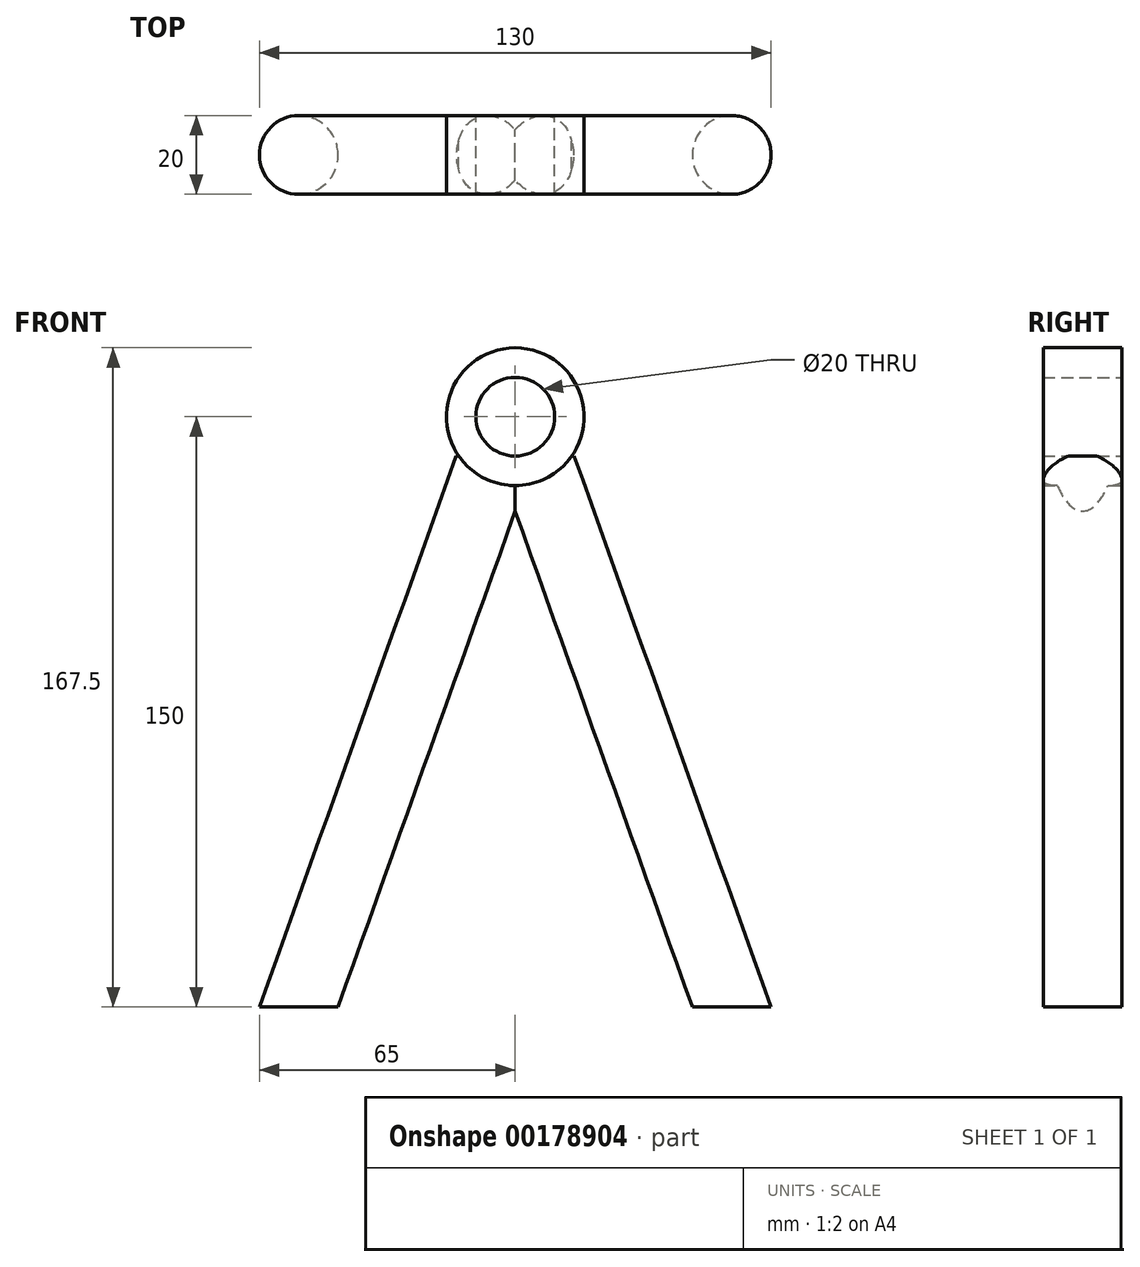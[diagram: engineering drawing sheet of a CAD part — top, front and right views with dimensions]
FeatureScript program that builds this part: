
annotation { "Feature Type Name" : "Feature", "Feature Type Description" : "" }
export const myFeature = defineFeature(function(context is Context, id is Id, definition is map)
    precondition{}
    {
        {
            var Q0;
            Q0=qCreatedBy(makeId("Top.planeOp"),FACE);
            var sketch = newSketch(context, id + "F0", { "sketchPlane" : qUnion([Q0])});
            skCircle(sketch, "E0", {"center": v(-55, 0) * mm, "radius": 10 * mm});
            skCircle(sketch, "E1", {"center": v(55, 0) * mm, "radius": 10 * mm});
            skSolve(sketch);
        }
        {
            var Q0;
            Q0=qCreatedBy(makeId("Front.planeOp"),FACE);
            var sketch = newSketch(context, id + "F1", { "sketchPlane" : qUnion([Q0])});
            skLineSegment(sketch, "E2", {"start": v(-55, 0) * mm, "end": v(-5, 140) * mm});
            skLineSegment(sketch, "E3", {"start": v(55, 0) * mm, "end": v(5, 140) * mm});
            skSolve(sketch);
        }
        {
            var Q0;
            Q0=makeQuery(id+"F0.imprint","IMPRINT",FACE,{"disambiguationData":[TD([[makeQuery(id+"F0.imprint","IMPRINT",EDGE,{"derivedFrom":sQuery(id+"F0.wireOp",EDGE,"E0")}),1.0]])]});
            var Q1;
            Q1=sQuery(id+"F1.wireOp",EDGE,"E2");
            sweep(context, id + "F2", {"profiles" : qUnion([Q0]), "path" : qUnion([Q1])});
        }
        {
            var Q0;
            Q0=makeQuery(id+"F0.imprint","IMPRINT",FACE,{"disambiguationData":[TD([[makeQuery(id+"F0.imprint","IMPRINT",EDGE,{"derivedFrom":sQuery(id+"F0.wireOp",EDGE,"E1")}),1.0]])]});
            var Q1;
            Q1=sQuery(id+"F1.wireOp",EDGE,"E3");
            sweep(context, id + "F3", {"operationType" : NewBodyOperationType.ADD, "profiles" : qUnion([Q0]), "path" : qUnion([Q1])});
        }
        {
            var Q0;
            Q0=qCreatedBy(makeId("Front.planeOp"),FACE);
            var sketch = newSketch(context, id + "F4", { "sketchPlane" : qUnion([Q0])});
            skCircle(sketch, "E4", {"center": v(0, 150) * mm, "radius": 17.5 * mm});
            skCircle(sketch, "E5", {"center": v(0, 150) * mm, "radius": 10 * mm});
            skSolve(sketch);
        }
        {
            var Q0;
            Q0=makeQuery(id+"F4.imprint","IMPRINT",FACE,{"disambiguationData":[TD([[makeQuery(id+"F4.imprint","IMPRINT",EDGE,{"derivedFrom":sQuery(id+"F4.wireOp",EDGE,"E4")}),1.0]])]});
            extrude(context, id + "F5", {"entities" : qUnion([Q0]), "operationType" : NewBodyOperationType.ADD, "endBound" : BoundingType.SYMMETRIC, "depth" : 20 * mm});
        }
    });
